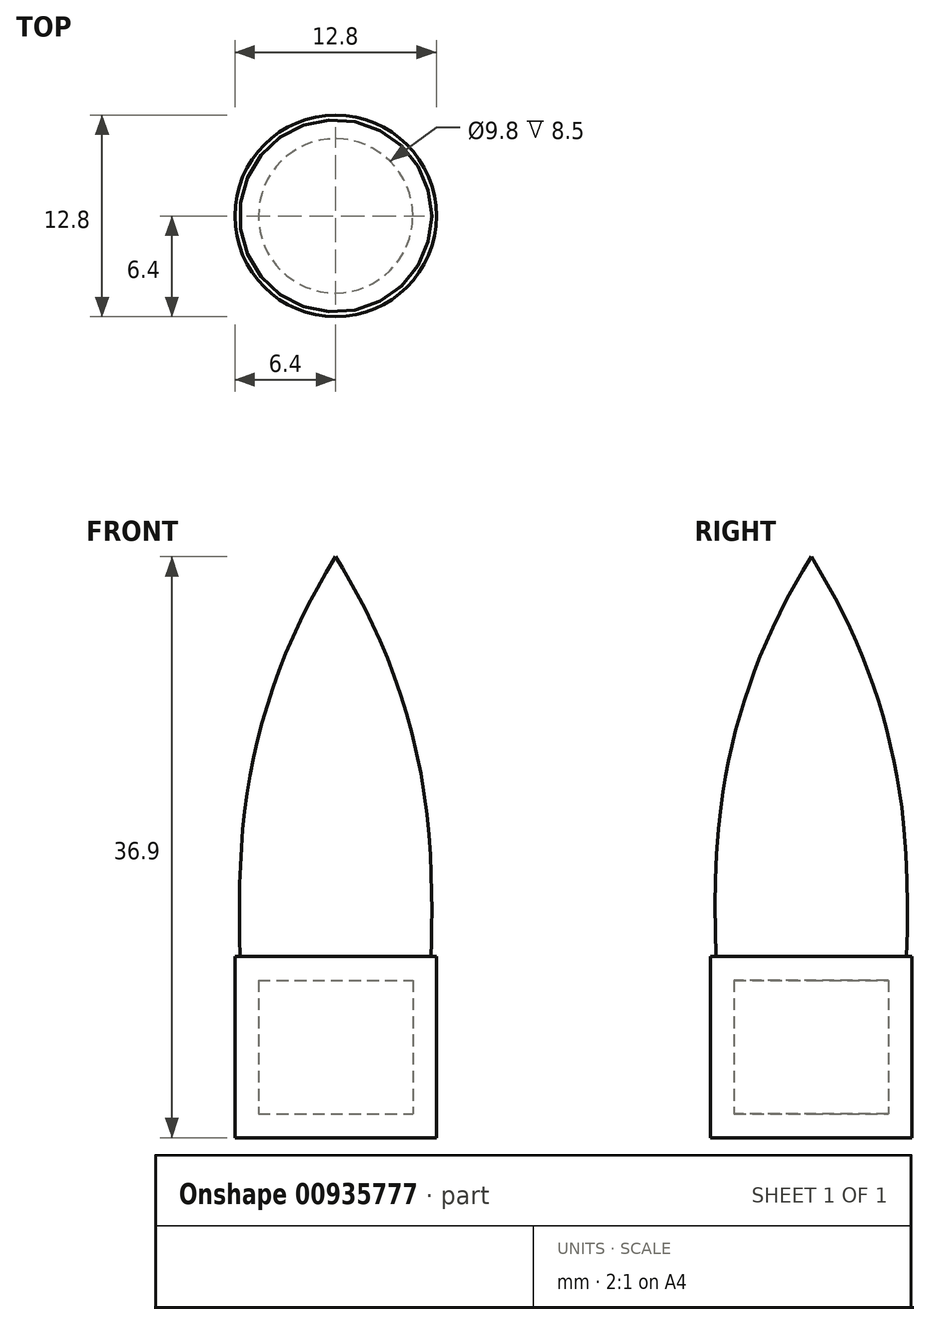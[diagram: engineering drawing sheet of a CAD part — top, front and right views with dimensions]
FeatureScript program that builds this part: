
annotation { "Feature Type Name" : "Feature", "Feature Type Description" : "" }
export const myFeature = defineFeature(function(context is Context, id is Id, definition is map)
    precondition{}
    {
        {
            var Q0;
            Q0=qCreatedBy(makeId("Front.planeOp"),FACE);
            var sketch = newSketch(context, id + "F0", { "sketchPlane" : qUnion([Q0])});
            skLineSegment(sketch, "E0", {"start": v(0, 0) * mm, "end": v(7.5, 0) * mm});
            skLineSegment(sketch, "E1", {"start": v(0, 0) * mm, "end": v(0, 30) * mm});
            skLineSegment(sketch, "E2.bottom", {"start": v(6.4, 1.5) * mm, "end": v(4.9, 1.5) * mm});
            skLineSegment(sketch, "E2.top", {"start": v(6.4, -10) * mm, "end": v(4.9, -10) * mm});
            skLineSegment(sketch, "E2.left", {"start": v(6.4, 1.5) * mm, "end": v(6.4, -10) * mm});
            skLineSegment(sketch, "E2.right", {"start": v(4.9, 1.5) * mm, "end": v(4.9, -10) * mm});
            skLineSegment(sketch, "E3.bottom", {"start": v(4.9, -10) * mm, "end": v(0, -10) * mm});
            skLineSegment(sketch, "E3.top", {"start": v(4.9, -8.5) * mm, "end": v(0, -8.5) * mm});
            skLineSegment(sketch, "E3.left", {"start": v(4.9, -10) * mm, "end": v(4.9, -8.5) * mm});
            skLineSegment(sketch, "E3.right", {"start": v(0, -10) * mm, "end": v(0, -8.5) * mm});
            skFitSpline(sketch, "E4", {"points": [v(0, 30) * mm, v(7.5, 0) * mm], "startDerivative": vector(8.55, -16.32) * mm, "endDerivative": vector(-1.31, -53.18) * mm});
            skFitSpline(sketch, "E5.0", {"points": [v(-1.33, 29.3) * mm, v(-0.6, 27.9) * mm, v(1.1, 25.02) * mm, v(3.66, 19.5) * mm, v(5.64, 11.73) * mm, v(6.1, 4.4) * mm, v(6, 0.04) * mm]});
            skSolve(sketch);
        }
        {
            var Q0;
            {var subQ7=sQuery(id+"F0.wireOp",EDGE,"997a9a27-7f6a-4ed5-ac33-0567eef3bca6");Q0=makeQuery(id+"F0.imprint","IMPRINT",FACE,{"disambiguationData":[TD([[makeQuery(id+"F0.imprint","IMPRINT",EDGE,{"derivedFrom":subQ7}),-1.0]])]});}
            var Q1;
            Q1=makeQuery(id+"F0.imprint","IMPRINT",FACE,{"disambiguationData":[TD([[makeQuery(id+"F0.imprint","IMPRINT",EDGE,{"derivedFrom":sQuery(id+"F0.wireOp",EDGE,"E3.bottom")}),-1.0]])]});
            var Q2;
            {var subQ1=sQuery(id+"F0.wireOp",EDGE,"E2.top");Q2=makeQuery(id+"F0.imprint","IMPRINT",FACE,{"disambiguationData":[TD([[makeQuery(id+"F0.imprint","IMPRINT",EDGE,{"derivedFrom":subQ1}),-1.0]])]});}
            var Q3;
            {var subQ0=sQuery(id+"F0.wireOp",EDGE,"c6cf19ad-7245-4cbd-8377-39daa56525c7.0");var subQ1=sQuery(id+"F0.wireOp",EDGE,"E0");var subQ2=makeQuery(id+"F0.imprint","INTERSECT",VERTEX,{"derivedFrom":[subQ1,subQ0]});Q3=makeQuery(id+"F0.imprint","IMPRINT",FACE,{"disambiguationData":[TD([[makeQuery(id+"F0.imprint","IMPRINT",EDGE,{"disambiguationData":[TD([[subQ2,1.0]])],"derivedFrom":subQ1}),1.0]])]});}
            var Q4;
            {var subQ0=sQuery(id+"F0.wireOp",EDGE,"c6cf19ad-7245-4cbd-8377-39daa56525c7.0");var subQ1=sQuery(id+"F0.wireOp",EDGE,"E0");var subQ2=makeQuery(id+"F0.imprint","INTERSECT",VERTEX,{"derivedFrom":[subQ1,subQ0]});Q4=makeQuery(id+"F0.imprint","IMPRINT",FACE,{"disambiguationData":[TD([[makeQuery(id+"F0.imprint","IMPRINT",EDGE,{"disambiguationData":[TD([[subQ2,-1.0]])],"derivedFrom":subQ1}),1.0]])]});}
            var Q5;
            Q5=sQuery(id+"F0.wireOp",EDGE,"E1");
            revolve(context, id + "F1", {"surfaceOperationType" : NewSurfaceOperationType.NEW, "entities" : qUnion([Q0, Q1, Q2, Q3, Q4]), "axis" : qUnion([Q5]), "revolveType" : RevolveType.FULL});
        }
    });
